# Revit family: Capsule Pool 3000-9000 вытяжной
name_source: partatom
category: Оборудование
units: mm (PartAtom-declared; Revit-internal decimal feet)

## family parameters
Всегда вертикально = Да
Классификация = Нет
На основе рабочей плоскости = Нет
Общий = Нет
При загрузке вырезать с полостями = Нет
Размер круглого соединителя = Использовать диаметр
Тип детали = Нормальный
Точка расчета площади = Нет

## types (7) — shared parameters
ADSK_Единица измерения = шт.
ADSK_Завод-изготовитель = ООО «Турков»
ADSK_Наименование = Система климатизации бассейнов Capsule Pool вытяжной модуль
ВВ_высота = 190 мм
ВВ_прит_X = 50 мм
Крепеж_У = 23 мм
Крепеж_Х = 3 мм
СЗ = 300 мм
Толщина_кр = 50 мм
zero-valued in all types: ADSK_Масса

## per-type parameters (varying)
| type | A1 длина | B1 глубина | C1 высота | ВВ_выт_Y | ВВ_выт_высота | ВВ_выт_ширина | ВВ_прит_высота | ВВ_прит_ширина | Коробочка_Х |
| Capsule Pool 3000 | 685 мм | 450 мм | 750 мм | 75 мм | 600 мм | 300 мм | 400 мм | 300 мм | 57 мм |
| Capsule Pool 4000 | 835 мм | 550 мм | 850 мм | 75 мм | 700 мм | 400 мм | 450 мм | 400 мм | 100 мм |
| Capsule Pool 5000 | 835 мм | 550 мм | 850 мм | 75 мм | 700 мм | 400 мм | 450 мм | 400 мм | 100 мм |
| Capsule Pool 6000 | 835 мм | 650 мм | 950 мм | 100 мм | 800 мм | 500 мм | 500 мм | 500 мм | 100 мм |
| Capsule Pool 7000 | 835 мм | 650 мм | 950 мм | 100 мм | 800 мм | 500 мм | 500 мм | 500 мм | 100 мм |
| Capsule Pool 8000 | 935 мм | 650 мм | 1050 мм | 100 мм | 900 мм | 500 мм | 600 мм | 500 мм | 100 мм |
| Capsule Pool 9000 | 935 мм | 650 мм | 1150 мм | 100 мм | 1000 мм | 500 мм | 600 мм | 500 мм | 100 мм |

note: column(s) folded — value = type name in every type: ADSK_Марка

## geometry (parser evidence)
native form markers: Sweep x4
no freeform markers — native parametric forms only
